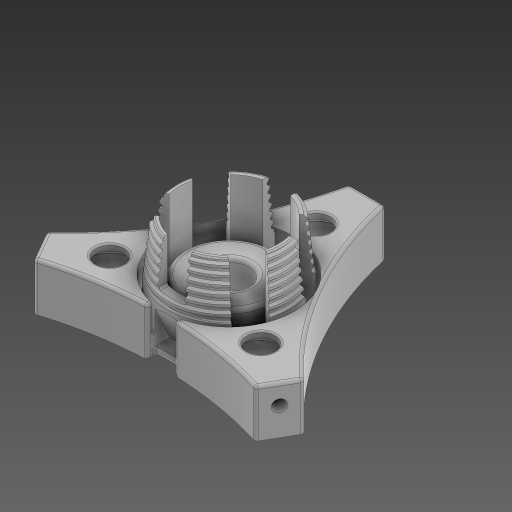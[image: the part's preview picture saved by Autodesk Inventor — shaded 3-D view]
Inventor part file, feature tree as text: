
AUTODESK INVENTOR PART (.ipt)
format: ipt  version: 2024 (Build 280153000, 153)  size: 1,676,288 bytes
history: native  units: mm
features: sketch x17, extrude x12, fillet x9, chamfer x3, hole x3, draft x2, helix x2, plane x2, pattern_circular x2, projected_geometry x2
ambient origin geometry x8: Origin, YZ Plane, XZ Plane, XY Plane, X Axis, Y Axis, Z Axis, Center Point
bodies: Solid1 (feature_tree)
feature tree (54):
  extrude  "Extrusion1"  Depth=29.5mm
  draft  "FaceDraft1"
  sketch  "Sketch2"  dims[d7=6.806784mm d8=0.55605mm]
  helix  "Coil1"  [1 undecoded]
  helix  "Coil2"  [1 undecoded]
  extrude  "Extrusion2"  Depth=0.55605mm
  extrude  "Extrusion3"  TaperAngle=0.0deg  [1 undecoded]
  fillet  "Fillet1"  [1 undecoded]
  chamfer  "Chamfer1"  Distance=0.3mm Angle=45.0deg
  plane  "Work Plane1"
  extrude  "Extrusion4"  TaperAngle=0.0deg  [1 undecoded]
  extrude  "Extrusion8"  Depth=60.0mm TaperAngle=360.0deg
  hole  "Hole2"  [1 undecoded]
  sketch  "Sketch13"  dims[d58=6.0mm d65=60.0mm d67=360.0deg]
  extrude  "Extrusion11"  Depth=10.0mm TaperAngle=0.0deg
  hole  "Bearing Hole"  [1 undecoded]
  pattern_circular  "Circular Pattern4"  Count=3 Angle=360.0deg
  extrude  "Extrusion13"  Depth=7.0mm TaperAngle=0.0deg
  sketch  "Sketch20"  dims[d126=7.204mm d127=6.0mm d128=10.379mm d129=8.89mm d130=90.0deg d131=8.0mm d132=20.594885mm d133=22.0mm d134=30.0mm d135=360.0deg]
  extrude  "Extrusion14"  Depth=1.55mm TaperAngle=45.0deg
  sketch  "Sketch18"  dims[d124=34.0mm]
  fillet  "Fillet9"  Radius=0.24mm
  chamfer  "Chamfer4"  [1 undecoded]
  chamfer  "Chamfer5"  Distance=0.5mm
  fillet  "Fillet11"  Radius=2.0mm
  draft  "FaceDraft2"
  fillet  "Fillet13"  Radius=34.767mm
  extrude  "Extrusion15"  Depth=0.5mm
  hole  "Hole5"  [1 undecoded]
  pattern_circular  "Circular Pattern5"  [2 undecoded]
  plane  "Work Plane4"
  extrude  "Extrusion16"  Depth=0.5mm
  fillet  "Fillet14"  Radius=30.0mm
  fillet  "Fillet16"  Radius=16.0mm
  extrude  "Extrusion17"  TaperAngle=0.0deg  [1 undecoded]
  extrude  "Extrusion19"  Depth=0.5mm
  fillet  "Fillet17"  Radius=0.4mm
  fillet  "Fillet18"  Radius=25.0mm
  fillet  "Fillet19"  Radius=22.0mm
  sketch  "Sketch1"  dims[d0=25.0mm d1=29.5mm d2=12.875mm d3=0.0mm d4=1.047198mm]
  projected_geometry  "Projected Loop1"
  sketch  "Sketch3"  dims[d9=6.806784mm]
  sketch  "Sketch4"  dims[d10=2.0mm d11=10.0mm d12=70.0mm d13=-1.047198mm d14=90.0deg d15=90.0deg d16=0.0mm d17=0.0mm d18=0.6mm]
  sketch  "Sketch5"  dims[d19=2.0mm d20=10.0mm d21=10.0mm d22=1.047198mm d23=90.0deg d24=90.0deg d25=0.0mm d26=0.0mm d27=0.0mm d28=0.0mm d29=0.0mm d30=0.0mm]
  sketch  "Sketch10"  dims[d31=0.6mm d32=0.3mm d33=2.0mm d34=45.0deg]
  sketch  "Sketch11"  dims[d36=-2.0mm d42=0.0mm d43=0.0mm]
  sketch  "Sketch15"  dims[d91=33.0mm d92=12.0mm d93=0.0mm]
  sketch  "Sketch17"  dims[d94=5.3mm d95=6.0mm d96=10.0mm d97=7.0mm d98=90.0deg d99=8.0mm d100=20.594885mm d122=10.0mm d123=0.0mm]
  sketch  "Sketch21"  dims[d146=11.34464mm d147=7.0mm d148=0.0mm]
  sketch  "Sketch22"  dims[d150=1.0mm d151=1.55mm d152=2.0mm d153=45.0deg]
  sketch  "Sketch25"  dims[d154=0.5mm d155=2.0mm d156=45.0deg d158=0.24mm]
  sketch  "Sketch26"  dims[d160=1.25mm d161=0.0mm d162=0.0mm]
  sketch  "Sketch28"  dims[d163=30.0deg d164=0.5mm d165=2.0mm d166=34.767mm d167=9.0mm d168=30.0deg d169=7.0mm d170=0.0mm d171=3.0mm d172=6.0mm d173=9.779mm d174=7.62mm d175=90.0deg d176=7.0mm d177=0.0mm d178=5.0mm d179=30.0mm d180=360.0deg d182=16.0mm d183=0.0mm d184=0.0mm d185=0.75mm d187=0.4mm d188=25.0mm d189=22.0mm d190=31.0mm d191=7.0mm d192=0.0mm d193=32.8mm d208=9.0mm d209=0.0mm d210=1.0mm d211=0.25mm d212=0.5mm d213=7.0mm d214=60.0mm d216=360.0deg]
  projected_geometry  "Project Cut Edges3"
note: 12 required parameter values undecoded (feature->parameter linkage not recoverable at this tier; creation-order binding heuristic only, values carry confidence <= 0.55)
